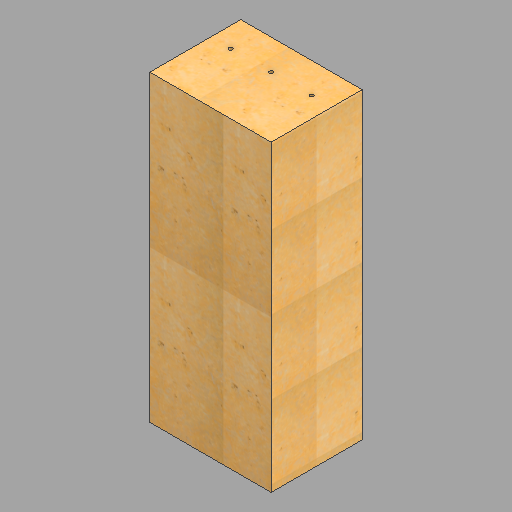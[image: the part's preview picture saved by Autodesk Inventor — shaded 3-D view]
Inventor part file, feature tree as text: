
AUTODESK INVENTOR PART (.ipt)
format: ipt  version: 2023 (Build 270158030, 158C)  size: 342,528 bytes
history: native  units: in
note: dims shown in document units (in); Inventor stores cm internally (conversion verified against a paired STEP export)
features: other x4, sketch x2, thicken_offset x2, projected_geometry x2, extrude x1
ambient origin geometry x8: Origin, YZ Plane, XZ Plane, XY Plane, X Axis, Y Axis, Z Axis, Center Point
bodies: Body1 (feature_tree)
feature tree (11):
  other  "Bottom"
  other  "Standard - Amber select"
  sketch  "Sketch1"  dims[d0=0.3937in d1=12.0in]
  thicken_offset  "Thicken1"
  thicken_offset  "Thicken2"
  extrude  "Extrusion1"  Depth=0.3937in
  other  "Bottom::Standard - Amber select"
  other  "TaggingFeature1"
  projected_geometry  "Projected Loop1"
  projected_geometry  "Projected Loop2"
  sketch  "Sketch2"  dims[d2=12.0in d3=12.0in d4=12.0in d5=12.0in d6=8.0in d7=16.0in d8=16.0in d9=8.0in d10=1.5in d11=12.5in d12=0.0in]
